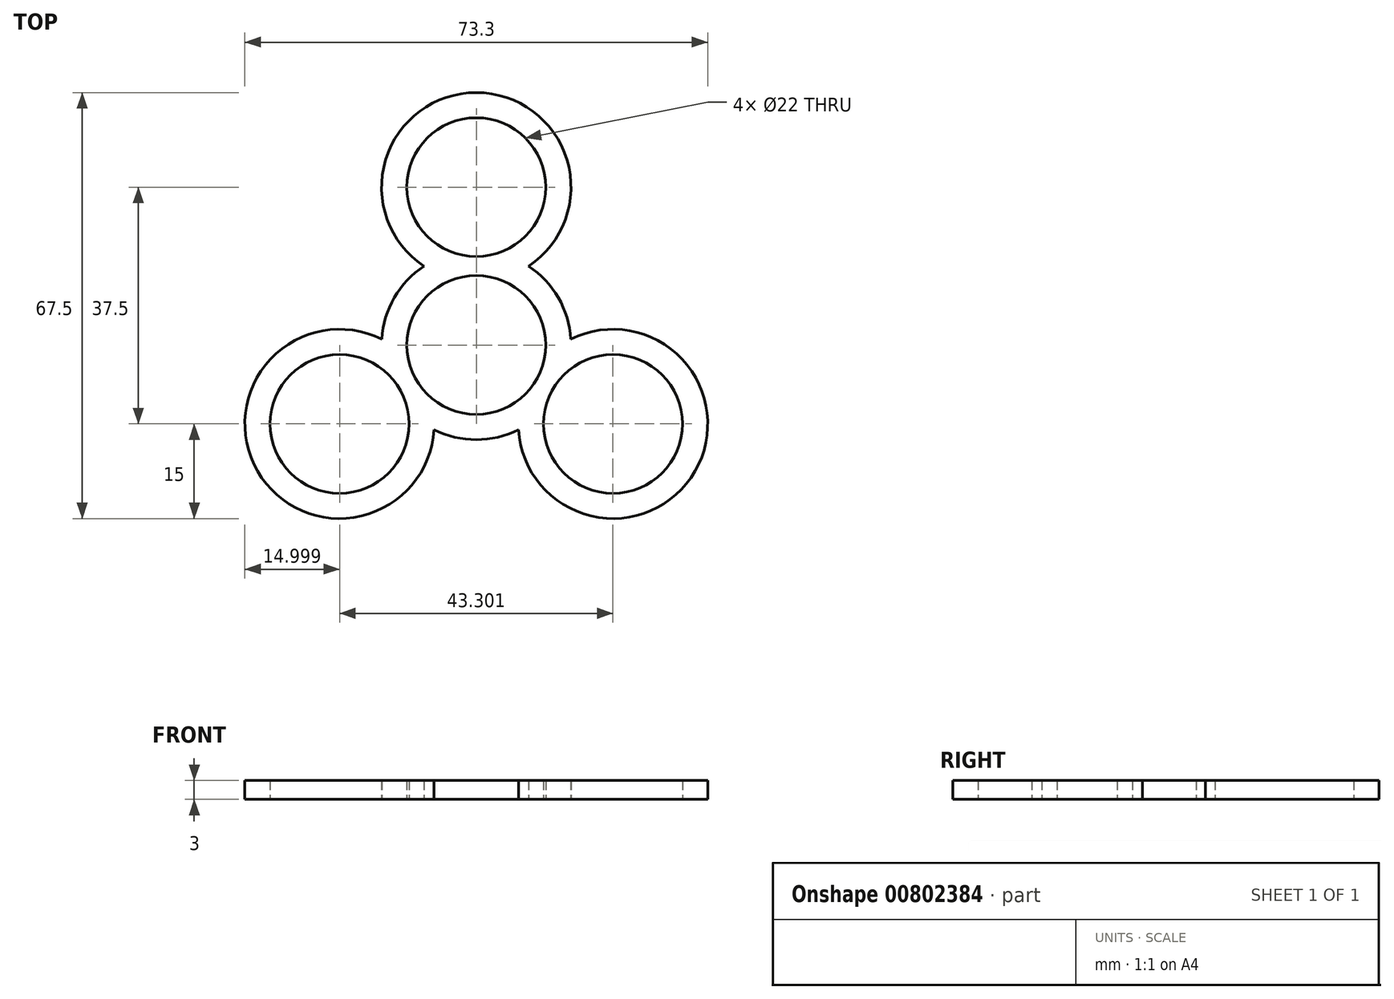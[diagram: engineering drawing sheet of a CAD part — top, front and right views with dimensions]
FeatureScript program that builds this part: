
annotation { "Feature Type Name" : "Feature", "Feature Type Description" : "" }
export const myFeature = defineFeature(function(context is Context, id is Id, definition is map)
    precondition{}
    {
        {
            var Q0;
            Q0=qCreatedBy(makeId("Top.planeOp"),FACE);
            var sketch = newSketch(context, id + "F0", { "sketchPlane" : qUnion([Q0])});
            skArc(sketch, "E0", {"start": v(9.53, 5.5) * mm, "mid": v(0, 11) * mm, "end": v(-9.53, 5.5) * mm});
            skCircle(sketch, "E1", {"center": v(0, 25) * mm, "radius": 11 * mm});
            skArc(sketch, "E2", {"start": v(8.3, 12.5) * mm, "mid": v(0, 40) * mm, "end": v(-8.3, 12.5) * mm});
            skArc(sketch, "E3.trimOffspring", {"start": v(-8.3, 12.5) * mm, "mid": v(-10.93, 10.27) * mm, "end": v(-13, 7.5) * mm});
            skArc(sketch, "E4.trimOffspring", {"start": v(13, 7.5) * mm, "mid": v(10.93, 10.27) * mm, "end": v(8.3, 12.5) * mm});
            skArc(sketch, "E5.1.0", {"start": v(-14.97, 0.93) * mm, "mid": v(-34.64, -20) * mm, "end": v(-6.68, -13.43) * mm});
            skCircle(sketch, "E5.1.1", {"center": v(-21.65, -12.5) * mm, "radius": 11 * mm});
            skArc(sketch, "E5.1.2", {"start": v(-9.53, 5.5) * mm, "mid": v(-9.53, -5.5) * mm, "end": v(0, -11) * mm});
            skArc(sketch, "E5.1.3", {"start": v(-13, 7.5) * mm, "mid": v(-14.36, 4.33) * mm, "end": v(-14.97, 0.93) * mm});
            skArc(sketch, "E5.1.4", {"start": v(-6.68, -13.43) * mm, "mid": v(-3.43, -14.6) * mm, "end": v(0, -15) * mm});
            skArc(sketch, "E5.2.0", {"start": v(6.68, -13.43) * mm, "mid": v(34.64, -20) * mm, "end": v(14.97, 0.93) * mm});
            skCircle(sketch, "E5.2.1", {"center": v(21.65, -12.5) * mm, "radius": 11 * mm});
            skArc(sketch, "E5.2.2", {"start": v(0, -11) * mm, "mid": v(9.53, -5.5) * mm, "end": v(9.53, 5.5) * mm});
            skArc(sketch, "E5.2.3", {"start": v(0, -15) * mm, "mid": v(3.43, -14.6) * mm, "end": v(6.68, -13.43) * mm});
            skArc(sketch, "E5.2.4", {"start": v(14.97, 0.93) * mm, "mid": v(14.36, 4.33) * mm, "end": v(13, 7.5) * mm});
            skSolve(sketch);
        }
        {
            var Q0;
            Q0 = qSketchRegion(id + "F0", true);
            extrude(context, id + "F1", {"entities" : qUnion([Q0]), "depth" : 3 * mm, "offsetDistance" : 25 * mm});
        }
    });
